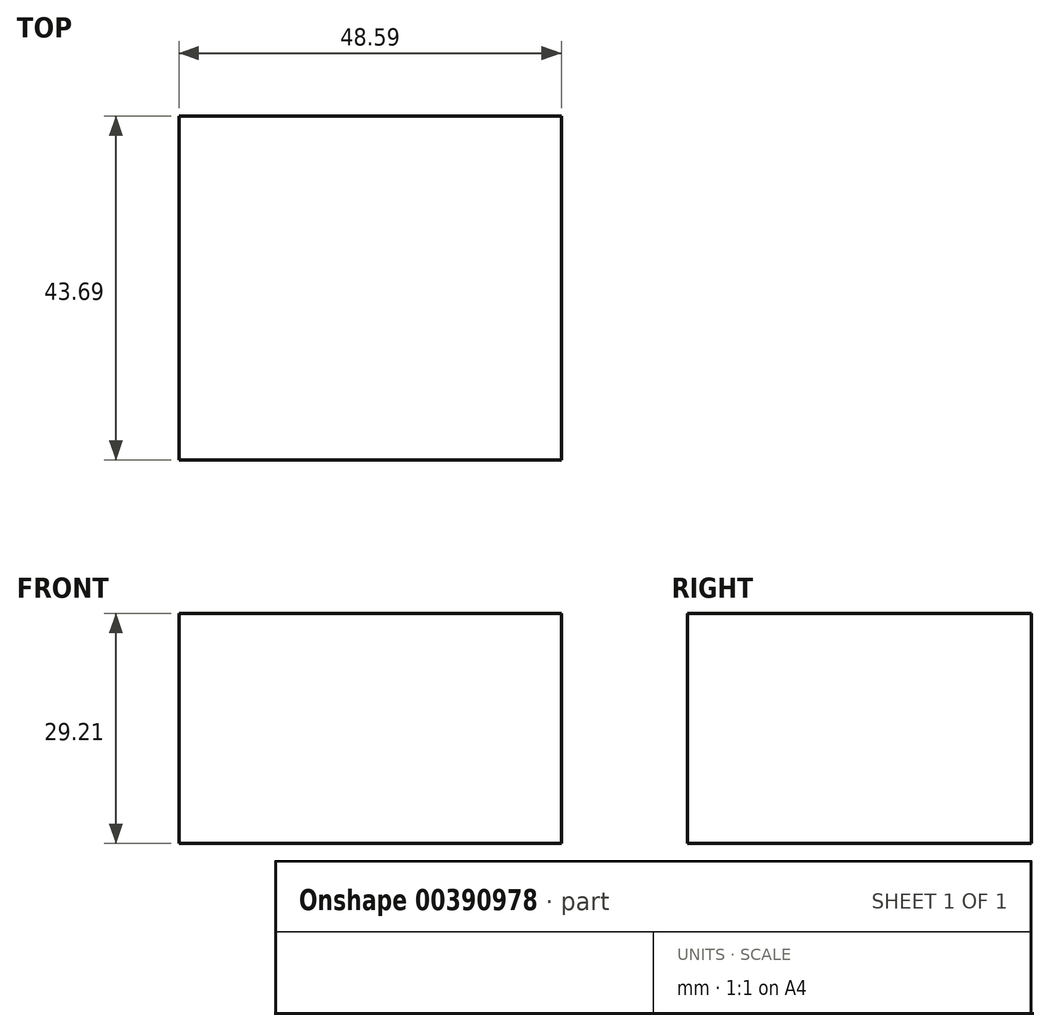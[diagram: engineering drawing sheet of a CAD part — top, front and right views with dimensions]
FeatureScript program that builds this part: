
annotation { "Feature Type Name" : "Feature", "Feature Type Description" : "" }
export const myFeature = defineFeature(function(context is Context, id is Id, definition is map)
    precondition{}
    {
        {
            var Q0;
            Q0=qCreatedBy(makeId("Top.planeOp"),FACE);
            var sketch = newSketch(context, id + "F0", { "sketchPlane" : qUnion([Q0])});
            skLineSegment(sketch, "E0.bottom", {"start": v(-55.28, 28.53) * mm, "end": v(-6.69, 28.53) * mm});
            skLineSegment(sketch, "E0.top", {"start": v(-55.28, -15.16) * mm, "end": v(-6.69, -15.16) * mm});
            skLineSegment(sketch, "E0.left", {"start": v(-55.28, 28.53) * mm, "end": v(-55.28, -15.16) * mm});
            skLineSegment(sketch, "E0.right", {"start": v(-6.69, 28.53) * mm, "end": v(-6.69, -15.16) * mm});
            skSolve(sketch);
        }
        {
            var Q0;
            Q0=makeQuery(id+"F0.imprint","IMPRINT",FACE,{"disambiguationData":[TD([[makeQuery(id+"F0.imprint","IMPRINT",EDGE,{"derivedFrom":sQuery(id+"F0.wireOp",EDGE,"E0.bottom")}),-1.0]])]});
            extrude(context, id + "F1", {"entities" : qUnion([Q0]), "depth" : 29.2 * mm});
        }
    });
